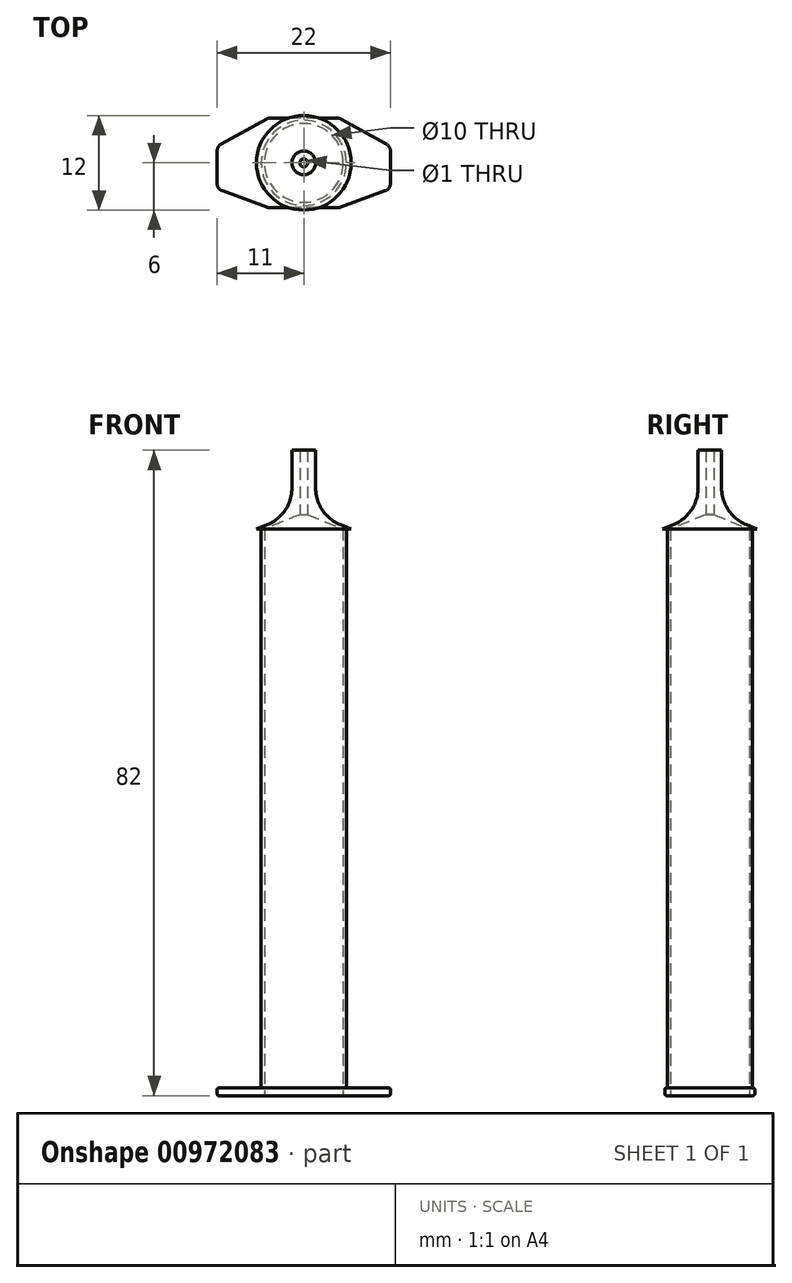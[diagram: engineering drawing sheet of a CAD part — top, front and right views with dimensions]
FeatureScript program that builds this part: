
annotation { "Feature Type Name" : "Feature", "Feature Type Description" : "" }
export const myFeature = defineFeature(function(context is Context, id is Id, definition is map)
    precondition{}
    {
        {
            var Q0;
            Q0=qCreatedBy(makeId("Top.planeOp"),FACE);
            var sketch = newSketch(context, id + "F0", { "sketchPlane" : qUnion([Q0])});
            skCircle(sketch, "E0", {"center": v(0, 0) * mm, "radius": 5 * mm});
            skCircle(sketch, "E1", {"center": v(0, 0) * mm, "radius": 5.4 * mm});
            skSolve(sketch);
        }
        {
            var Q0;
            Q0=makeQuery(id+"F0.imprint","IMPRINT",FACE,{"disambiguationData":[TD([[makeQuery(id+"F0.imprint","IMPRINT",EDGE,{"derivedFrom":sQuery(id+"F0.wireOp",EDGE,"E0")}),-1.0]])]});
            extrude(context, id + "F1", {"entities" : qUnion([Q0]), "depth" : 62 * mm, "offsetDistance" : 25 * mm, "hasSecondDirection" : true, "secondDirectionOppositeDirection" : true, "secondDirectionDepth" : 9 * mm});
        }
        {
            var Q0;
            Q0=qCreatedBy(makeId("Front.planeOp"),FACE);
            var sketch = newSketch(context, id + "F2", { "sketchPlane" : qUnion([Q0])});
            skLineSegment(sketch, "E2", {"start": v(4.64, 62.54) * mm, "end": v(6, 62) * mm});
            skLineSegment(sketch, "E3", {"start": v(0, 62) * mm, "end": v(6, 62) * mm});
            skLineSegment(sketch, "E4", {"start": v(0.5, 63.8) * mm, "end": v(5, 62) * mm});
            skLineSegment(sketch, "E5", {"start": v(0.5, 63.8) * mm, "end": v(0.5, 72) * mm});
            skLineSegment(sketch, "E6", {"start": v(1.5, 67.19) * mm, "end": v(1.5, 72) * mm});
            skLineSegment(sketch, "E7", {"start": v(0.5, 72) * mm, "end": v(1.5, 72) * mm});
            skLineSegment(sketch, "E8", {"start": v(0, 62) * mm, "end": v(0, 62.89) * mm});
            skPoint(sketch, "E9.visualSharp", {"position": v(1.5, 63.8) * mm});
            skArc(sketch, "E9.filletArc", {"start": v(1.5, 67.19) * mm, "mid": v(2.36, 64.38) * mm, "end": v(4.64, 62.54) * mm});
            skSolve(sketch);
        }
        {
            var Q0;
            {var subQ2=sQuery(id+"F2.wireOp",EDGE,"E2");Q0=makeQuery(id+"F2.imprint","IMPRINT",FACE,{"disambiguationData":[TD([[makeQuery(id+"F2.imprint","IMPRINT",EDGE,{"derivedFrom":subQ2}),-1.0]])]});}
            var Q1;
            Q1=sQuery(id+"F2.wireOp",EDGE,"E8");
            revolve(context, id + "F3", {"operationType" : NewBodyOperationType.ADD, "surfaceOperationType" : NewSurfaceOperationType.NEW, "entities" : qUnion([Q0]), "axis" : qUnion([Q1]), "revolveType" : RevolveType.FULL});
        }
        {
            var Q0;
            Q0=makeQuery(id+"F1.opExtrude","CAP_FACE",FACE,{"disambiguationData":[OSD([sQuery(id+"F0.wireOp",EDGE,"E0"),sQuery(id+"F0.wireOp",EDGE,"E1")])],"isStart":true});
            cPlane(context, id + "F4", {"entities" : qUnion([Q0]), "cplaneType" : CPlaneType.OFFSET, "offset" : 0 * mm, "width" : 150 * mm, "height" : 150 * mm});
        }
        {
            var Q0;
            Q0=qCreatedBy(id+"F4.planeOp",FACE);
            var sketch = newSketch(context, id + "F5", { "sketchPlane" : qUnion([Q0])});
            skLineSegment(sketch, "E10", {"start": v(4.5, 5.7) * mm, "end": v(11, 3.31) * mm});
            skLineSegment(sketch, "E11.MirrorCS", {"start": v(4.5, -5.7) * mm, "end": v(11, -2.11) * mm});
            skLineSegment(sketch, "E12.MirrorCS", {"start": v(-4.5, 5.7) * mm, "end": v(-11, 3.31) * mm});
            skLineSegment(sketch, "E13.MirrorCS", {"start": v(-4.5, -5.7) * mm, "end": v(-11, -2.11) * mm});
            skCircle(sketch, "E14", {"center": v(0, 0) * mm, "radius": 5 * mm});
            skLineSegment(sketch, "E15", {"start": v(4.5, 5.7) * mm, "end": v(-4.5, 5.7) * mm});
            skLineSegment(sketch, "E16", {"start": v(4.5, -5.7) * mm, "end": v(-4.5, -5.7) * mm});
            skLineSegment(sketch, "E17", {"start": v(11, 3.31) * mm, "end": v(11, -2.11) * mm});
            skLineSegment(sketch, "E18", {"start": v(-11, 3.31) * mm, "end": v(-11, -2.11) * mm});
            skSolve(sketch);
        }
        {
            var Q0;
            Q0=makeQuery(id+"F5.imprint","IMPRINT",FACE,{"disambiguationData":[TD([[makeQuery(id+"F5.imprint","IMPRINT",EDGE,{"derivedFrom":sQuery(id+"F5.wireOp",EDGE,"Z6K4M87V-DVPl-VIz8-pgWM-HxpkCWdUFoVx.top")}),1.0]])]});
            var Q1;
            Q1=makeQuery(id+"F5.imprint","IMPRINT",FACE,{"disambiguationData":[TD([[makeQuery(id+"F5.imprint","IMPRINT",EDGE,{"derivedFrom":sQuery(id+"F5.wireOp",EDGE,"E10")}),-1.0]])]});
            extrude(context, id + "F6", {"entities" : qUnion([Q0, Q1]), "operationType" : NewBodyOperationType.ADD, "depth" : 1 * mm, "offsetDistance" : 25 * mm});
        }
        {
            var Q0;
            Q0=makeQuery(id+"F6.opExtrude","SWEPT_EDGE",EDGE,{"disambiguationData":[OSD([sQuery(id+"F5.wireOp",EDGE,"df01a680-1bff-42a6-ba12-da2397d9a9860.MirrorCS"),sQuery(id+"F5.wireOp",EDGE,"E12.MirrorCS")])]});
            var Q1;
            Q1=makeQuery(id+"F6.opExtrude","SWEPT_EDGE",EDGE,{"disambiguationData":[OSD([sQuery(id+"F5.wireOp",EDGE,"07e45aba-89c8-4687-9971-865d9c13b24f0.MirrorCS"),sQuery(id+"F5.wireOp",EDGE,"E13.MirrorCS")])]});
            var Q2;
            Q2=makeQuery(id+"F6.opExtrude","SWEPT_EDGE",EDGE,{"disambiguationData":[OSD([sQuery(id+"F5.wireOp",EDGE,"Z6K4M87V-DVPl-VIz8-pgWM-HxpkCWdUFoVx.right"),sQuery(id+"F5.wireOp",EDGE,"E11.MirrorCS")])]});
            var Q3;
            Q3=makeQuery(id+"F6.opExtrude","SWEPT_EDGE",EDGE,{"disambiguationData":[OSD([sQuery(id+"F5.wireOp",EDGE,"6886a79b-2828-4634-8f31-eee592987a7b0.MirrorCS"),sQuery(id+"F5.wireOp",EDGE,"E10")])]});
            fillet(context, id + "F7", {"entities" : qUnion([Q0, Q1, Q2, Q3]), "radius" : 1 * mm, "tangentPropagation" : true, "allowEdgeOverflow" : false});
        }
        {
            var Q0;
            Q0=makeQuery(id+"F6.opExtrude","CAP_EDGE",EDGE,{"disambiguationData":[OSD([sQuery(id+"F5.wireOp",EDGE,"E12.MirrorCS")])],"isStart":false});
            var Q1;
            {var subQ0=sQuery(id+"F5.wireOp",EDGE,"E15");var subQ1=sQuery(id+"F5.wireOp",EDGE,"E12.MirrorCS");Q1=makeQuery(id+"F7.opFillet","BLEND_EDGE",EDGE,{"blendedFrom":[makeQuery(id+"F6.opExtrude","SWEPT_EDGE",EDGE,{"disambiguationData":[OSD([subQ1,subQ0])]}),makeQuery(id+"F6.opExtrude","CAP_FACE",FACE,{"disambiguationData":[OSD([sQuery(id+"F5.wireOp",EDGE,"E10"),sQuery(id+"F5.wireOp",EDGE,"E11.MirrorCS"),subQ1,sQuery(id+"F5.wireOp",EDGE,"E13.MirrorCS"),sQuery(id+"F5.wireOp",EDGE,"E14"),subQ0,sQuery(id+"F5.wireOp",EDGE,"E16"),sQuery(id+"F5.wireOp",EDGE,"E17"),sQuery(id+"F5.wireOp",EDGE,"E18")])],"isStart":false})],"blendedInto":[makeQuery(id+"F6.opExtrude","CAP_FACE",FACE,{"disambiguationData":[OSD([sQuery(id+"F5.wireOp",EDGE,"E10"),sQuery(id+"F5.wireOp",EDGE,"E11.MirrorCS"),subQ1,sQuery(id+"F5.wireOp",EDGE,"E13.MirrorCS"),sQuery(id+"F5.wireOp",EDGE,"E14"),subQ0,sQuery(id+"F5.wireOp",EDGE,"E16"),sQuery(id+"F5.wireOp",EDGE,"E17"),sQuery(id+"F5.wireOp",EDGE,"E18")])],"isStart":false})]});}
            var Q2;
            Q2=makeQuery(id+"F6.opExtrude","CAP_EDGE",EDGE,{"disambiguationData":[OSD([sQuery(id+"F5.wireOp",EDGE,"E15")])],"isStart":false});
            var Q3;
            Q3=makeQuery(id+"F6.opExtrude","CAP_EDGE",EDGE,{"disambiguationData":[OSD([sQuery(id+"F5.wireOp",EDGE,"E18")])],"isStart":false});
            var Q4;
            {var subQ0=sQuery(id+"F5.wireOp",EDGE,"E18");var subQ1=sQuery(id+"F5.wireOp",EDGE,"E12.MirrorCS");Q4=makeQuery(id+"F7.opFillet","BLEND_EDGE",EDGE,{"blendedFrom":[makeQuery(id+"F6.opExtrude","SWEPT_EDGE",EDGE,{"disambiguationData":[OSD([subQ1,subQ0])]}),makeQuery(id+"F6.opExtrude","CAP_FACE",FACE,{"disambiguationData":[OSD([sQuery(id+"F5.wireOp",EDGE,"E10"),sQuery(id+"F5.wireOp",EDGE,"E11.MirrorCS"),subQ1,sQuery(id+"F5.wireOp",EDGE,"E13.MirrorCS"),sQuery(id+"F5.wireOp",EDGE,"E14"),sQuery(id+"F5.wireOp",EDGE,"E15"),sQuery(id+"F5.wireOp",EDGE,"E16"),sQuery(id+"F5.wireOp",EDGE,"E17"),subQ0])],"isStart":false})],"blendedInto":[makeQuery(id+"F6.opExtrude","CAP_FACE",FACE,{"disambiguationData":[OSD([sQuery(id+"F5.wireOp",EDGE,"E10"),sQuery(id+"F5.wireOp",EDGE,"E11.MirrorCS"),subQ1,sQuery(id+"F5.wireOp",EDGE,"E13.MirrorCS"),sQuery(id+"F5.wireOp",EDGE,"E14"),sQuery(id+"F5.wireOp",EDGE,"E15"),sQuery(id+"F5.wireOp",EDGE,"E16"),sQuery(id+"F5.wireOp",EDGE,"E17"),subQ0])],"isStart":false})]});}
            var Q5;
            {var subQ0=sQuery(id+"F5.wireOp",EDGE,"E18");var subQ1=sQuery(id+"F5.wireOp",EDGE,"E13.MirrorCS");Q5=makeQuery(id+"F7.opFillet","BLEND_EDGE",EDGE,{"blendedFrom":[makeQuery(id+"F6.opExtrude","SWEPT_EDGE",EDGE,{"disambiguationData":[OSD([subQ1,subQ0])]}),makeQuery(id+"F6.opExtrude","CAP_FACE",FACE,{"disambiguationData":[OSD([sQuery(id+"F5.wireOp",EDGE,"E10"),sQuery(id+"F5.wireOp",EDGE,"E11.MirrorCS"),sQuery(id+"F5.wireOp",EDGE,"E12.MirrorCS"),subQ1,sQuery(id+"F5.wireOp",EDGE,"E14"),sQuery(id+"F5.wireOp",EDGE,"E15"),sQuery(id+"F5.wireOp",EDGE,"E16"),sQuery(id+"F5.wireOp",EDGE,"E17"),subQ0])],"isStart":false})],"blendedInto":[makeQuery(id+"F6.opExtrude","CAP_FACE",FACE,{"disambiguationData":[OSD([sQuery(id+"F5.wireOp",EDGE,"E10"),sQuery(id+"F5.wireOp",EDGE,"E11.MirrorCS"),sQuery(id+"F5.wireOp",EDGE,"E12.MirrorCS"),subQ1,sQuery(id+"F5.wireOp",EDGE,"E14"),sQuery(id+"F5.wireOp",EDGE,"E15"),sQuery(id+"F5.wireOp",EDGE,"E16"),sQuery(id+"F5.wireOp",EDGE,"E17"),subQ0])],"isStart":false})]});}
            var Q6;
            Q6=makeQuery(id+"F6.opExtrude","CAP_EDGE",EDGE,{"disambiguationData":[OSD([sQuery(id+"F5.wireOp",EDGE,"E13.MirrorCS")])],"isStart":false});
            var Q7;
            {var subQ0=sQuery(id+"F5.wireOp",EDGE,"E16");var subQ1=sQuery(id+"F5.wireOp",EDGE,"E13.MirrorCS");Q7=makeQuery(id+"F7.opFillet","BLEND_EDGE",EDGE,{"blendedFrom":[makeQuery(id+"F6.opExtrude","SWEPT_EDGE",EDGE,{"disambiguationData":[OSD([subQ1,subQ0])]}),makeQuery(id+"F6.opExtrude","CAP_FACE",FACE,{"disambiguationData":[OSD([sQuery(id+"F5.wireOp",EDGE,"E10"),sQuery(id+"F5.wireOp",EDGE,"E11.MirrorCS"),sQuery(id+"F5.wireOp",EDGE,"E12.MirrorCS"),subQ1,sQuery(id+"F5.wireOp",EDGE,"E14"),sQuery(id+"F5.wireOp",EDGE,"E15"),subQ0,sQuery(id+"F5.wireOp",EDGE,"E17"),sQuery(id+"F5.wireOp",EDGE,"E18")])],"isStart":false})],"blendedInto":[makeQuery(id+"F6.opExtrude","CAP_FACE",FACE,{"disambiguationData":[OSD([sQuery(id+"F5.wireOp",EDGE,"E10"),sQuery(id+"F5.wireOp",EDGE,"E11.MirrorCS"),sQuery(id+"F5.wireOp",EDGE,"E12.MirrorCS"),subQ1,sQuery(id+"F5.wireOp",EDGE,"E14"),sQuery(id+"F5.wireOp",EDGE,"E15"),subQ0,sQuery(id+"F5.wireOp",EDGE,"E17"),sQuery(id+"F5.wireOp",EDGE,"E18")])],"isStart":false})]});}
            var Q8;
            Q8=makeQuery(id+"F6.opExtrude","CAP_EDGE",EDGE,{"disambiguationData":[OSD([sQuery(id+"F5.wireOp",EDGE,"E16")])],"isStart":false});
            var Q9;
            {var subQ0=sQuery(id+"F5.wireOp",EDGE,"E16");var subQ1=sQuery(id+"F5.wireOp",EDGE,"E11.MirrorCS");Q9=makeQuery(id+"F7.opFillet","BLEND_EDGE",EDGE,{"blendedFrom":[makeQuery(id+"F6.opExtrude","SWEPT_EDGE",EDGE,{"disambiguationData":[OSD([subQ1,subQ0])]}),makeQuery(id+"F6.opExtrude","CAP_FACE",FACE,{"disambiguationData":[OSD([sQuery(id+"F5.wireOp",EDGE,"E10"),subQ1,sQuery(id+"F5.wireOp",EDGE,"E12.MirrorCS"),sQuery(id+"F5.wireOp",EDGE,"E13.MirrorCS"),sQuery(id+"F5.wireOp",EDGE,"E14"),sQuery(id+"F5.wireOp",EDGE,"E15"),subQ0,sQuery(id+"F5.wireOp",EDGE,"E17"),sQuery(id+"F5.wireOp",EDGE,"E18")])],"isStart":false})],"blendedInto":[makeQuery(id+"F6.opExtrude","CAP_FACE",FACE,{"disambiguationData":[OSD([sQuery(id+"F5.wireOp",EDGE,"E10"),subQ1,sQuery(id+"F5.wireOp",EDGE,"E12.MirrorCS"),sQuery(id+"F5.wireOp",EDGE,"E13.MirrorCS"),sQuery(id+"F5.wireOp",EDGE,"E14"),sQuery(id+"F5.wireOp",EDGE,"E15"),subQ0,sQuery(id+"F5.wireOp",EDGE,"E17"),sQuery(id+"F5.wireOp",EDGE,"E18")])],"isStart":false})]});}
            var Q10;
            Q10=makeQuery(id+"F6.opExtrude","CAP_EDGE",EDGE,{"disambiguationData":[OSD([sQuery(id+"F5.wireOp",EDGE,"E11.MirrorCS")])],"isStart":false});
            var Q11;
            Q11=makeQuery(id+"F6.opExtrude","CAP_EDGE",EDGE,{"disambiguationData":[OSD([sQuery(id+"F5.wireOp",EDGE,"E10")])],"isStart":false});
            var Q12;
            {var subQ0=sQuery(id+"F5.wireOp",EDGE,"E15");var subQ1=sQuery(id+"F5.wireOp",EDGE,"E10");Q12=makeQuery(id+"F7.opFillet","BLEND_EDGE",EDGE,{"blendedFrom":[makeQuery(id+"F6.opExtrude","SWEPT_EDGE",EDGE,{"disambiguationData":[OSD([subQ1,subQ0])]}),makeQuery(id+"F6.opExtrude","CAP_FACE",FACE,{"disambiguationData":[OSD([subQ1,sQuery(id+"F5.wireOp",EDGE,"E11.MirrorCS"),sQuery(id+"F5.wireOp",EDGE,"E12.MirrorCS"),sQuery(id+"F5.wireOp",EDGE,"E13.MirrorCS"),sQuery(id+"F5.wireOp",EDGE,"E14"),subQ0,sQuery(id+"F5.wireOp",EDGE,"E16"),sQuery(id+"F5.wireOp",EDGE,"E17"),sQuery(id+"F5.wireOp",EDGE,"E18")])],"isStart":false})],"blendedInto":[makeQuery(id+"F6.opExtrude","CAP_FACE",FACE,{"disambiguationData":[OSD([subQ1,sQuery(id+"F5.wireOp",EDGE,"E11.MirrorCS"),sQuery(id+"F5.wireOp",EDGE,"E12.MirrorCS"),sQuery(id+"F5.wireOp",EDGE,"E13.MirrorCS"),sQuery(id+"F5.wireOp",EDGE,"E14"),subQ0,sQuery(id+"F5.wireOp",EDGE,"E16"),sQuery(id+"F5.wireOp",EDGE,"E17"),sQuery(id+"F5.wireOp",EDGE,"E18")])],"isStart":false})]});}
            var Q13;
            {var subQ0=sQuery(id+"F5.wireOp",EDGE,"E17");var subQ1=sQuery(id+"F5.wireOp",EDGE,"E10");Q13=makeQuery(id+"F7.opFillet","BLEND_EDGE",EDGE,{"blendedFrom":[makeQuery(id+"F6.opExtrude","SWEPT_EDGE",EDGE,{"disambiguationData":[OSD([subQ1,subQ0])]}),makeQuery(id+"F6.opExtrude","CAP_FACE",FACE,{"disambiguationData":[OSD([subQ1,sQuery(id+"F5.wireOp",EDGE,"E11.MirrorCS"),sQuery(id+"F5.wireOp",EDGE,"E12.MirrorCS"),sQuery(id+"F5.wireOp",EDGE,"E13.MirrorCS"),sQuery(id+"F5.wireOp",EDGE,"E14"),sQuery(id+"F5.wireOp",EDGE,"E15"),sQuery(id+"F5.wireOp",EDGE,"E16"),subQ0,sQuery(id+"F5.wireOp",EDGE,"E18")])],"isStart":false})],"blendedInto":[makeQuery(id+"F6.opExtrude","CAP_FACE",FACE,{"disambiguationData":[OSD([subQ1,sQuery(id+"F5.wireOp",EDGE,"E11.MirrorCS"),sQuery(id+"F5.wireOp",EDGE,"E12.MirrorCS"),sQuery(id+"F5.wireOp",EDGE,"E13.MirrorCS"),sQuery(id+"F5.wireOp",EDGE,"E14"),sQuery(id+"F5.wireOp",EDGE,"E15"),sQuery(id+"F5.wireOp",EDGE,"E16"),subQ0,sQuery(id+"F5.wireOp",EDGE,"E18")])],"isStart":false})]});}
            var Q14;
            Q14=makeQuery(id+"F6.opExtrude","CAP_EDGE",EDGE,{"disambiguationData":[OSD([sQuery(id+"F5.wireOp",EDGE,"E17")])],"isStart":false});
            var Q15;
            {var subQ0=sQuery(id+"F5.wireOp",EDGE,"E17");var subQ1=sQuery(id+"F5.wireOp",EDGE,"E11.MirrorCS");Q15=makeQuery(id+"F7.opFillet","BLEND_EDGE",EDGE,{"blendedFrom":[makeQuery(id+"F6.opExtrude","SWEPT_EDGE",EDGE,{"disambiguationData":[OSD([subQ1,subQ0])]}),makeQuery(id+"F6.opExtrude","CAP_FACE",FACE,{"disambiguationData":[OSD([sQuery(id+"F5.wireOp",EDGE,"E10"),subQ1,sQuery(id+"F5.wireOp",EDGE,"E12.MirrorCS"),sQuery(id+"F5.wireOp",EDGE,"E13.MirrorCS"),sQuery(id+"F5.wireOp",EDGE,"E14"),sQuery(id+"F5.wireOp",EDGE,"E15"),sQuery(id+"F5.wireOp",EDGE,"E16"),subQ0,sQuery(id+"F5.wireOp",EDGE,"E18")])],"isStart":false})],"blendedInto":[makeQuery(id+"F6.opExtrude","CAP_FACE",FACE,{"disambiguationData":[OSD([sQuery(id+"F5.wireOp",EDGE,"E10"),subQ1,sQuery(id+"F5.wireOp",EDGE,"E12.MirrorCS"),sQuery(id+"F5.wireOp",EDGE,"E13.MirrorCS"),sQuery(id+"F5.wireOp",EDGE,"E14"),sQuery(id+"F5.wireOp",EDGE,"E15"),sQuery(id+"F5.wireOp",EDGE,"E16"),subQ0,sQuery(id+"F5.wireOp",EDGE,"E18")])],"isStart":false})]});}
            fillet(context, id + "F8", {"entities" : qUnion([Q0, Q1, Q2, Q3, Q4, Q5, Q6, Q7, Q8, Q9, Q10, Q11, Q12, Q13, Q14, Q15]), "radius" : .2 * mm, "tangentPropagation" : true, "allowEdgeOverflow" : false});
        }
        {
            var Q0;
            {var subQ0=sQuery(id+"F5.wireOp",EDGE,"E17");var subQ1=sQuery(id+"F5.wireOp",EDGE,"E10");Q0=makeQuery(id+"F7.opFillet","BLEND_EDGE",EDGE,{"blendedFrom":[makeQuery(id+"F6.opExtrude","SWEPT_EDGE",EDGE,{"disambiguationData":[OSD([subQ1,subQ0])]}),makeQuery(id+"F6.opExtrude","CAP_FACE",FACE,{"disambiguationData":[OSD([subQ1,sQuery(id+"F5.wireOp",EDGE,"E11.MirrorCS"),sQuery(id+"F5.wireOp",EDGE,"E12.MirrorCS"),sQuery(id+"F5.wireOp",EDGE,"E13.MirrorCS"),sQuery(id+"F5.wireOp",EDGE,"E14"),sQuery(id+"F5.wireOp",EDGE,"E15"),sQuery(id+"F5.wireOp",EDGE,"E16"),subQ0,sQuery(id+"F5.wireOp",EDGE,"E18")])],"isStart":true})],"blendedInto":[makeQuery(id+"F6.opExtrude","CAP_FACE",FACE,{"disambiguationData":[OSD([subQ1,sQuery(id+"F5.wireOp",EDGE,"E11.MirrorCS"),sQuery(id+"F5.wireOp",EDGE,"E12.MirrorCS"),sQuery(id+"F5.wireOp",EDGE,"E13.MirrorCS"),sQuery(id+"F5.wireOp",EDGE,"E14"),sQuery(id+"F5.wireOp",EDGE,"E15"),sQuery(id+"F5.wireOp",EDGE,"E16"),subQ0,sQuery(id+"F5.wireOp",EDGE,"E18")])],"isStart":true})]});}
            var Q1;
            Q1=makeQuery(id+"F6.opExtrude","CAP_EDGE",EDGE,{"disambiguationData":[OSD([sQuery(id+"F5.wireOp",EDGE,"E17")])],"isStart":true});
            var Q2;
            {var subQ0=sQuery(id+"F5.wireOp",EDGE,"E17");var subQ1=sQuery(id+"F5.wireOp",EDGE,"E11.MirrorCS");Q2=makeQuery(id+"F7.opFillet","BLEND_EDGE",EDGE,{"blendedFrom":[makeQuery(id+"F6.opExtrude","SWEPT_EDGE",EDGE,{"disambiguationData":[OSD([subQ1,subQ0])]}),makeQuery(id+"F6.opExtrude","CAP_FACE",FACE,{"disambiguationData":[OSD([sQuery(id+"F5.wireOp",EDGE,"E10"),subQ1,sQuery(id+"F5.wireOp",EDGE,"E12.MirrorCS"),sQuery(id+"F5.wireOp",EDGE,"E13.MirrorCS"),sQuery(id+"F5.wireOp",EDGE,"E14"),sQuery(id+"F5.wireOp",EDGE,"E15"),sQuery(id+"F5.wireOp",EDGE,"E16"),subQ0,sQuery(id+"F5.wireOp",EDGE,"E18")])],"isStart":true})],"blendedInto":[makeQuery(id+"F6.opExtrude","CAP_FACE",FACE,{"disambiguationData":[OSD([sQuery(id+"F5.wireOp",EDGE,"E10"),subQ1,sQuery(id+"F5.wireOp",EDGE,"E12.MirrorCS"),sQuery(id+"F5.wireOp",EDGE,"E13.MirrorCS"),sQuery(id+"F5.wireOp",EDGE,"E14"),sQuery(id+"F5.wireOp",EDGE,"E15"),sQuery(id+"F5.wireOp",EDGE,"E16"),subQ0,sQuery(id+"F5.wireOp",EDGE,"E18")])],"isStart":true})]});}
            var Q3;
            Q3=makeQuery(id+"F6.opExtrude","CAP_EDGE",EDGE,{"disambiguationData":[OSD([sQuery(id+"F5.wireOp",EDGE,"E11.MirrorCS")])],"isStart":true});
            var Q4;
            {var subQ0=sQuery(id+"F5.wireOp",EDGE,"E16");var subQ1=sQuery(id+"F5.wireOp",EDGE,"E11.MirrorCS");Q4=makeQuery(id+"F7.opFillet","BLEND_EDGE",EDGE,{"blendedFrom":[makeQuery(id+"F6.opExtrude","SWEPT_EDGE",EDGE,{"disambiguationData":[OSD([subQ1,subQ0])]}),makeQuery(id+"F6.opExtrude","CAP_FACE",FACE,{"disambiguationData":[OSD([sQuery(id+"F5.wireOp",EDGE,"E10"),subQ1,sQuery(id+"F5.wireOp",EDGE,"E12.MirrorCS"),sQuery(id+"F5.wireOp",EDGE,"E13.MirrorCS"),sQuery(id+"F5.wireOp",EDGE,"E14"),sQuery(id+"F5.wireOp",EDGE,"E15"),subQ0,sQuery(id+"F5.wireOp",EDGE,"E17"),sQuery(id+"F5.wireOp",EDGE,"E18")])],"isStart":true})],"blendedInto":[makeQuery(id+"F6.opExtrude","CAP_FACE",FACE,{"disambiguationData":[OSD([sQuery(id+"F5.wireOp",EDGE,"E10"),subQ1,sQuery(id+"F5.wireOp",EDGE,"E12.MirrorCS"),sQuery(id+"F5.wireOp",EDGE,"E13.MirrorCS"),sQuery(id+"F5.wireOp",EDGE,"E14"),sQuery(id+"F5.wireOp",EDGE,"E15"),subQ0,sQuery(id+"F5.wireOp",EDGE,"E17"),sQuery(id+"F5.wireOp",EDGE,"E18")])],"isStart":true})]});}
            var Q5;
            Q5=makeQuery(id+"F6.opExtrude","CAP_EDGE",EDGE,{"disambiguationData":[OSD([sQuery(id+"F5.wireOp",EDGE,"E16")])],"isStart":true});
            var Q6;
            {var subQ0=sQuery(id+"F5.wireOp",EDGE,"E16");var subQ1=sQuery(id+"F5.wireOp",EDGE,"E13.MirrorCS");Q6=makeQuery(id+"F7.opFillet","BLEND_EDGE",EDGE,{"blendedFrom":[makeQuery(id+"F6.opExtrude","SWEPT_EDGE",EDGE,{"disambiguationData":[OSD([subQ1,subQ0])]}),makeQuery(id+"F6.opExtrude","CAP_FACE",FACE,{"disambiguationData":[OSD([sQuery(id+"F5.wireOp",EDGE,"E10"),sQuery(id+"F5.wireOp",EDGE,"E11.MirrorCS"),sQuery(id+"F5.wireOp",EDGE,"E12.MirrorCS"),subQ1,sQuery(id+"F5.wireOp",EDGE,"E14"),sQuery(id+"F5.wireOp",EDGE,"E15"),subQ0,sQuery(id+"F5.wireOp",EDGE,"E17"),sQuery(id+"F5.wireOp",EDGE,"E18")])],"isStart":true})],"blendedInto":[makeQuery(id+"F6.opExtrude","CAP_FACE",FACE,{"disambiguationData":[OSD([sQuery(id+"F5.wireOp",EDGE,"E10"),sQuery(id+"F5.wireOp",EDGE,"E11.MirrorCS"),sQuery(id+"F5.wireOp",EDGE,"E12.MirrorCS"),subQ1,sQuery(id+"F5.wireOp",EDGE,"E14"),sQuery(id+"F5.wireOp",EDGE,"E15"),subQ0,sQuery(id+"F5.wireOp",EDGE,"E17"),sQuery(id+"F5.wireOp",EDGE,"E18")])],"isStart":true})]});}
            var Q7;
            {var subQ0=sQuery(id+"F5.wireOp",EDGE,"E18");var subQ1=sQuery(id+"F5.wireOp",EDGE,"E13.MirrorCS");Q7=makeQuery(id+"F7.opFillet","BLEND_EDGE",EDGE,{"blendedFrom":[makeQuery(id+"F6.opExtrude","SWEPT_EDGE",EDGE,{"disambiguationData":[OSD([subQ1,subQ0])]}),makeQuery(id+"F6.opExtrude","CAP_FACE",FACE,{"disambiguationData":[OSD([sQuery(id+"F5.wireOp",EDGE,"E10"),sQuery(id+"F5.wireOp",EDGE,"E11.MirrorCS"),sQuery(id+"F5.wireOp",EDGE,"E12.MirrorCS"),subQ1,sQuery(id+"F5.wireOp",EDGE,"E14"),sQuery(id+"F5.wireOp",EDGE,"E15"),sQuery(id+"F5.wireOp",EDGE,"E16"),sQuery(id+"F5.wireOp",EDGE,"E17"),subQ0])],"isStart":true})],"blendedInto":[makeQuery(id+"F6.opExtrude","CAP_FACE",FACE,{"disambiguationData":[OSD([sQuery(id+"F5.wireOp",EDGE,"E10"),sQuery(id+"F5.wireOp",EDGE,"E11.MirrorCS"),sQuery(id+"F5.wireOp",EDGE,"E12.MirrorCS"),subQ1,sQuery(id+"F5.wireOp",EDGE,"E14"),sQuery(id+"F5.wireOp",EDGE,"E15"),sQuery(id+"F5.wireOp",EDGE,"E16"),sQuery(id+"F5.wireOp",EDGE,"E17"),subQ0])],"isStart":true})]});}
            var Q8;
            Q8=makeQuery(id+"F6.opExtrude","CAP_EDGE",EDGE,{"disambiguationData":[OSD([sQuery(id+"F5.wireOp",EDGE,"E13.MirrorCS")])],"isStart":true});
            var Q9;
            Q9=makeQuery(id+"F6.opExtrude","CAP_EDGE",EDGE,{"disambiguationData":[OSD([sQuery(id+"F5.wireOp",EDGE,"E10")])],"isStart":true});
            var Q10;
            Q10=makeQuery(id+"F6.opExtrude","CAP_EDGE",EDGE,{"disambiguationData":[OSD([sQuery(id+"F5.wireOp",EDGE,"E15")])],"isStart":true});
            var Q11;
            Q11=makeQuery(id+"F6.opExtrude","CAP_EDGE",EDGE,{"disambiguationData":[OSD([sQuery(id+"F5.wireOp",EDGE,"E18")])],"isStart":true});
            var Q12;
            {var subQ0=sQuery(id+"F5.wireOp",EDGE,"E18");var subQ1=sQuery(id+"F5.wireOp",EDGE,"E12.MirrorCS");Q12=makeQuery(id+"F7.opFillet","BLEND_EDGE",EDGE,{"blendedFrom":[makeQuery(id+"F6.opExtrude","SWEPT_EDGE",EDGE,{"disambiguationData":[OSD([subQ1,subQ0])]}),makeQuery(id+"F6.opExtrude","CAP_FACE",FACE,{"disambiguationData":[OSD([sQuery(id+"F5.wireOp",EDGE,"E10"),sQuery(id+"F5.wireOp",EDGE,"E11.MirrorCS"),subQ1,sQuery(id+"F5.wireOp",EDGE,"E13.MirrorCS"),sQuery(id+"F5.wireOp",EDGE,"E14"),sQuery(id+"F5.wireOp",EDGE,"E15"),sQuery(id+"F5.wireOp",EDGE,"E16"),sQuery(id+"F5.wireOp",EDGE,"E17"),subQ0])],"isStart":true})],"blendedInto":[makeQuery(id+"F6.opExtrude","CAP_FACE",FACE,{"disambiguationData":[OSD([sQuery(id+"F5.wireOp",EDGE,"E10"),sQuery(id+"F5.wireOp",EDGE,"E11.MirrorCS"),subQ1,sQuery(id+"F5.wireOp",EDGE,"E13.MirrorCS"),sQuery(id+"F5.wireOp",EDGE,"E14"),sQuery(id+"F5.wireOp",EDGE,"E15"),sQuery(id+"F5.wireOp",EDGE,"E16"),sQuery(id+"F5.wireOp",EDGE,"E17"),subQ0])],"isStart":true})]});}
            var Q13;
            {var subQ0=sQuery(id+"F5.wireOp",EDGE,"E15");var subQ1=sQuery(id+"F5.wireOp",EDGE,"E12.MirrorCS");Q13=makeQuery(id+"F7.opFillet","BLEND_EDGE",EDGE,{"blendedFrom":[makeQuery(id+"F6.opExtrude","SWEPT_EDGE",EDGE,{"disambiguationData":[OSD([subQ1,subQ0])]}),makeQuery(id+"F6.opExtrude","CAP_FACE",FACE,{"disambiguationData":[OSD([sQuery(id+"F5.wireOp",EDGE,"E10"),sQuery(id+"F5.wireOp",EDGE,"E11.MirrorCS"),subQ1,sQuery(id+"F5.wireOp",EDGE,"E13.MirrorCS"),sQuery(id+"F5.wireOp",EDGE,"E14"),subQ0,sQuery(id+"F5.wireOp",EDGE,"E16"),sQuery(id+"F5.wireOp",EDGE,"E17"),sQuery(id+"F5.wireOp",EDGE,"E18")])],"isStart":true})],"blendedInto":[makeQuery(id+"F6.opExtrude","CAP_FACE",FACE,{"disambiguationData":[OSD([sQuery(id+"F5.wireOp",EDGE,"E10"),sQuery(id+"F5.wireOp",EDGE,"E11.MirrorCS"),subQ1,sQuery(id+"F5.wireOp",EDGE,"E13.MirrorCS"),sQuery(id+"F5.wireOp",EDGE,"E14"),subQ0,sQuery(id+"F5.wireOp",EDGE,"E16"),sQuery(id+"F5.wireOp",EDGE,"E17"),sQuery(id+"F5.wireOp",EDGE,"E18")])],"isStart":true})]});}
            var Q14;
            {var subQ0=sQuery(id+"F5.wireOp",EDGE,"E15");var subQ1=sQuery(id+"F5.wireOp",EDGE,"E10");Q14=makeQuery(id+"F7.opFillet","BLEND_EDGE",EDGE,{"blendedFrom":[makeQuery(id+"F6.opExtrude","SWEPT_EDGE",EDGE,{"disambiguationData":[OSD([subQ1,subQ0])]}),makeQuery(id+"F6.opExtrude","CAP_FACE",FACE,{"disambiguationData":[OSD([subQ1,sQuery(id+"F5.wireOp",EDGE,"E11.MirrorCS"),sQuery(id+"F5.wireOp",EDGE,"E12.MirrorCS"),sQuery(id+"F5.wireOp",EDGE,"E13.MirrorCS"),sQuery(id+"F5.wireOp",EDGE,"E14"),subQ0,sQuery(id+"F5.wireOp",EDGE,"E16"),sQuery(id+"F5.wireOp",EDGE,"E17"),sQuery(id+"F5.wireOp",EDGE,"E18")])],"isStart":true})],"blendedInto":[makeQuery(id+"F6.opExtrude","CAP_FACE",FACE,{"disambiguationData":[OSD([subQ1,sQuery(id+"F5.wireOp",EDGE,"E11.MirrorCS"),sQuery(id+"F5.wireOp",EDGE,"E12.MirrorCS"),sQuery(id+"F5.wireOp",EDGE,"E13.MirrorCS"),sQuery(id+"F5.wireOp",EDGE,"E14"),subQ0,sQuery(id+"F5.wireOp",EDGE,"E16"),sQuery(id+"F5.wireOp",EDGE,"E17"),sQuery(id+"F5.wireOp",EDGE,"E18")])],"isStart":true})]});}
            var Q15;
            Q15=makeQuery(id+"F6.opExtrude","CAP_EDGE",EDGE,{"disambiguationData":[OSD([sQuery(id+"F5.wireOp",EDGE,"E12.MirrorCS")])],"isStart":true});
            fillet(context, id + "F9", {"entities" : qUnion([Q0, Q1, Q2, Q3, Q4, Q5, Q6, Q7, Q8, Q9, Q10, Q11, Q12, Q13, Q14, Q15]), "radius" : .2 * mm, "tangentPropagation" : true, "allowEdgeOverflow" : false});
        }
    });
